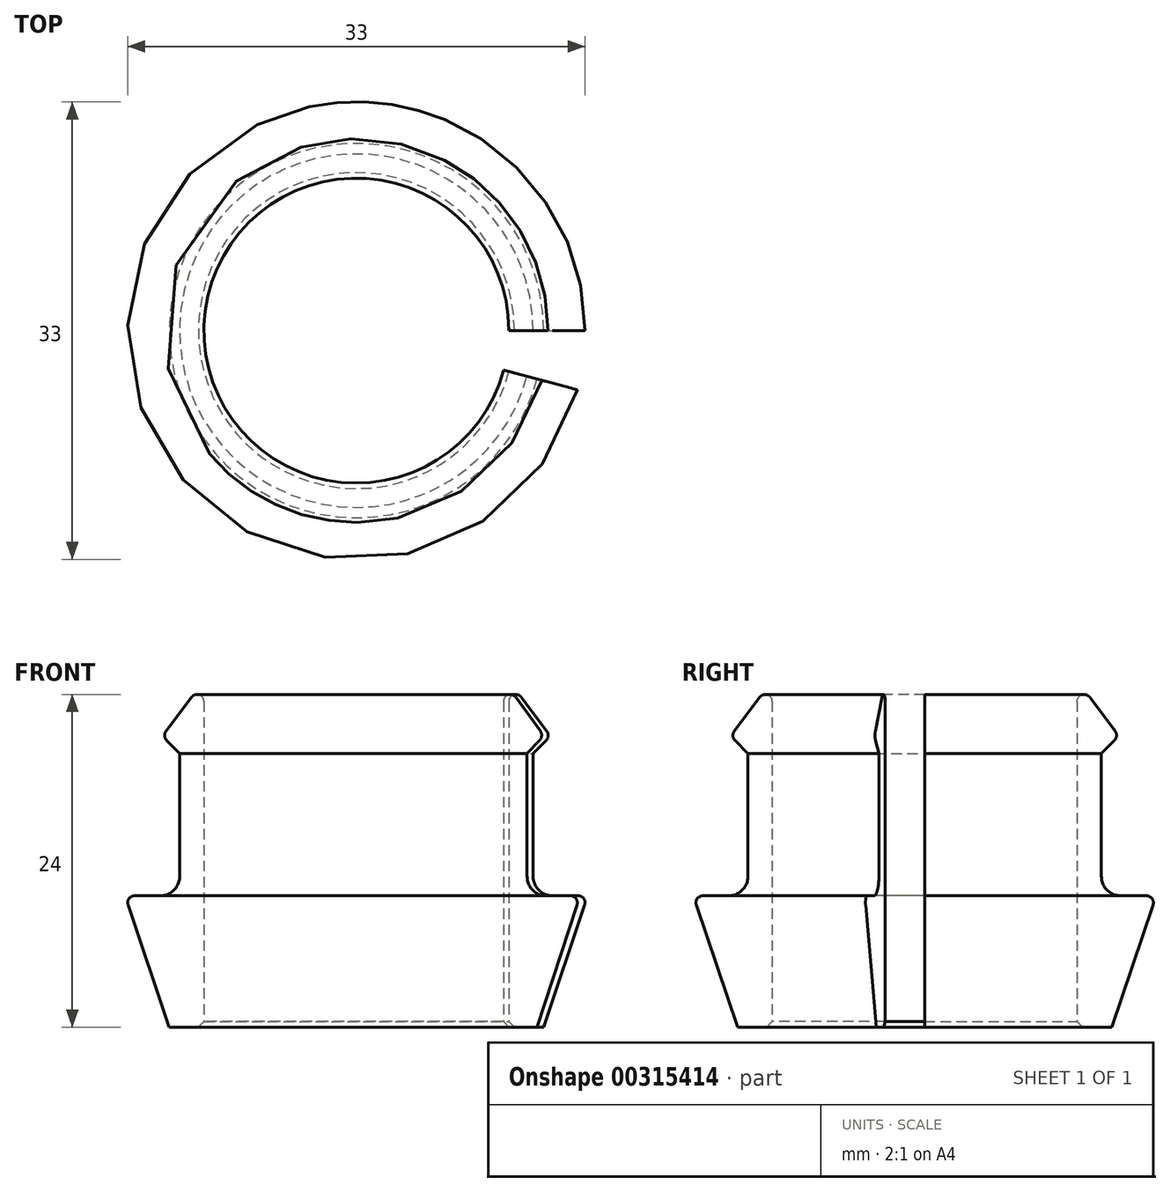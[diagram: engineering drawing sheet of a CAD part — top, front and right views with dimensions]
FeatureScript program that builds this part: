
annotation { "Feature Type Name" : "Feature", "Feature Type Description" : "" }
export const myFeature = defineFeature(function(context is Context, id is Id, definition is map)
    precondition{}
    {
        {
            var Q0;
            Q0=qCreatedBy(makeId("Front.planeOp"),FACE);
            var sketch = newSketch(context, id + "F0", { "sketchPlane" : qUnion([Q0])});
            skLineSegment(sketch, "E0", {"start": v(0, -21.72) * mm, "end": v(0, 27.6) * mm, "construction": true});
            skLineSegment(sketch, "E1", {"start": v(11, 10.96) * mm, "end": v(11, -14.04) * mm});
            skLineSegment(sketch, "E2", {"start": v(11, -14.04) * mm, "end": v(13.5, -14.04) * mm});
            skLineSegment(sketch, "E3", {"start": v(13.5, -14.04) * mm, "end": v(16.7, -4.57) * mm});
            skLineSegment(sketch, "E4", {"start": v(16.7, -4.57) * mm, "end": v(12.75, -4.57) * mm});
            skLineSegment(sketch, "E5", {"start": v(12.75, -4.57) * mm, "end": v(12.75, 5.7) * mm});
            skLineSegment(sketch, "E6", {"start": v(14, 6.96) * mm, "end": v(11, 10.96) * mm});
            skLineSegment(sketch, "E7", {"start": v(14, 6.96) * mm, "end": v(12.75, 5.7) * mm});
            skSolve(sketch);
        }
        {
            var Q0;
            Q0 = qSketchRegion(id + "F0", true);
            var Q1;
            Q1=sQuery(id+"F0.wireOp",EDGE,"E0");
            revolve(context, id + "F1", {"entities" : qUnion([Q0]), "axis" : qUnion([Q1]), "revolveType" : RevolveType.ONE_DIRECTION, "angle" : 345 * degree});
        }
        {
            var Q0;
            Q0=makeQuery(id+"F1.opRevolve","SWEPT_EDGE",EDGE,{"disambiguationData":[OSD([sQuery(id+"F0.wireOp",EDGE,"E4"),sQuery(id+"F0.wireOp",EDGE,"E5")])]});
            fillet(context, id + "F2", {"entities" : qUnion([Q0]), "radius" : 1.4 * mm, "tangentPropagation" : true, "allowEdgeOverflow" : false});
        }
        {
            var Q0;
            Q0=makeQuery(id+"F1.opRevolve","SWEPT_EDGE",EDGE,{"disambiguationData":[OSD([sQuery(id+"F0.wireOp",EDGE,"E3"),sQuery(id+"F0.wireOp",EDGE,"E4")])]});
            var Q1;
            Q1=makeQuery(id+"F1.opRevolve","SWEPT_EDGE",EDGE,{"disambiguationData":[OSD([sQuery(id+"F0.wireOp",EDGE,"sSSy9y7l-qLEd-wN3G-f1UG-PpuoiEZqKbcN"),sQuery(id+"F0.wireOp",EDGE,"E6"),sQuery(id+"F0.wireOp",EDGE,"E7")])]});
            var Q2;
            Q2=makeQuery(id+"F1.opRevolve","SWEPT_EDGE",EDGE,{"disambiguationData":[OSD([sQuery(id+"F0.wireOp",EDGE,"E1"),sQuery(id+"F0.wireOp",EDGE,"E6")])]});
            fillet(context, id + "F3", {"entities" : qUnion([Q0, Q1, Q2]), "radius" : 0.5 * mm, "tangentPropagation" : true, "allowEdgeOverflow" : false});
        }
        {
            var Q0;
            Q0=makeQuery(id+"F1.opRevolve","SWEPT_EDGE",EDGE,{"disambiguationData":[OSD([sQuery(id+"F0.wireOp",EDGE,"E1"),sQuery(id+"F0.wireOp",EDGE,"E2")])]});
            chamfer(context, id + "F4", {"entities" : qUnion([Q0]), "width" : 0.4 * mm, "tangentPropagation" : true});
        }
    });
